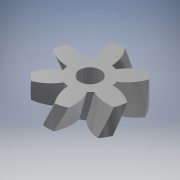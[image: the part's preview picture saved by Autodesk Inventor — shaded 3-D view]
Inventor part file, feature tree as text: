
AUTODESK INVENTOR PART (.ipt)
format: ipt  version: 2017 SP1 (Build 210196100, 196)  size: 459,264 bytes
history: native  units: mm (DEFAULTED — no unit token found)
features: plane x3, other x3, sketch x3, extrude x2
ambient origin geometry x8: Origin, YZ Plane, XZ Plane, XY Plane, X Axis, Y Axis, Z Axis, Center Point
bodies: Solid1 (feature_tree)
feature tree (11):
  extrude  "Extrusion1"  Depth=10.0mm TaperAngle=0.0deg
  plane  "Work Plane2"
  plane  "Work Plane8"
  plane  "Work Plane9"
  other  "Engrenage cylindrique"
  extrude  "Extrusion2"  Depth=10.0mm TaperAngle=0.0deg
  sketch  "Sketch1"  dims[d0=34.188431mm d1=10.0mm d2=0.0mm]
  sketch  "Sketch2"  dims[d3=26.24881mm d4=10.0mm d5=0.0mm d16=26.24881mm d17=0.0mm d34=30.0deg d39=0.0mm d41=0.0mm d43=26.24881mm d46=26.24881mm d47=0.0mm d48=0.0mm d49=8.5mm d50=20.0mm d51=0.0mm]
  other  "Srf1"
  sketch  "Esquisse3"
  other  "Diamètre primitif"
